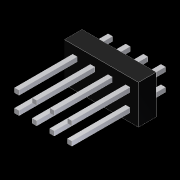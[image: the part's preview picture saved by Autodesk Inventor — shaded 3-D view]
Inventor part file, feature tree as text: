
AUTODESK INVENTOR PART (.ipt)
format: ipt  version: 2012 (Build 160160000, 160)  size: 126,464 bytes
history: native  units: in
note: dims shown in document units (in); Inventor stores cm internally (conversion verified against a paired STEP export)
features: extrude x3, sketch x1, pattern_linear x1
ambient origin geometry x8: Origin, YZ Plane, XZ Plane, XY Plane, X Axis, Y Axis, Z Axis, Center Point
bodies: Solid1 (feature_tree)
feature tree (5):
  sketch  "Sketch1"  dims[d0=0.1in d1=0.0in d2=0.33in d3=0.0in d4=0.2in d5=0.0in d6=1.5748in d8=0.1in d9=0.7874in d11=0.1in]
  extrude  "Extrusion1"  Depth=0.33in TaperAngle=0.0deg
  extrude  "Extrusion2"  Depth=0.2in TaperAngle=0.0deg
  extrude  "Extrusion3"  Depth=1.5748in
  pattern_linear  "Rectangular Pattern1"  Count1=2 Spacing1=0.1in
